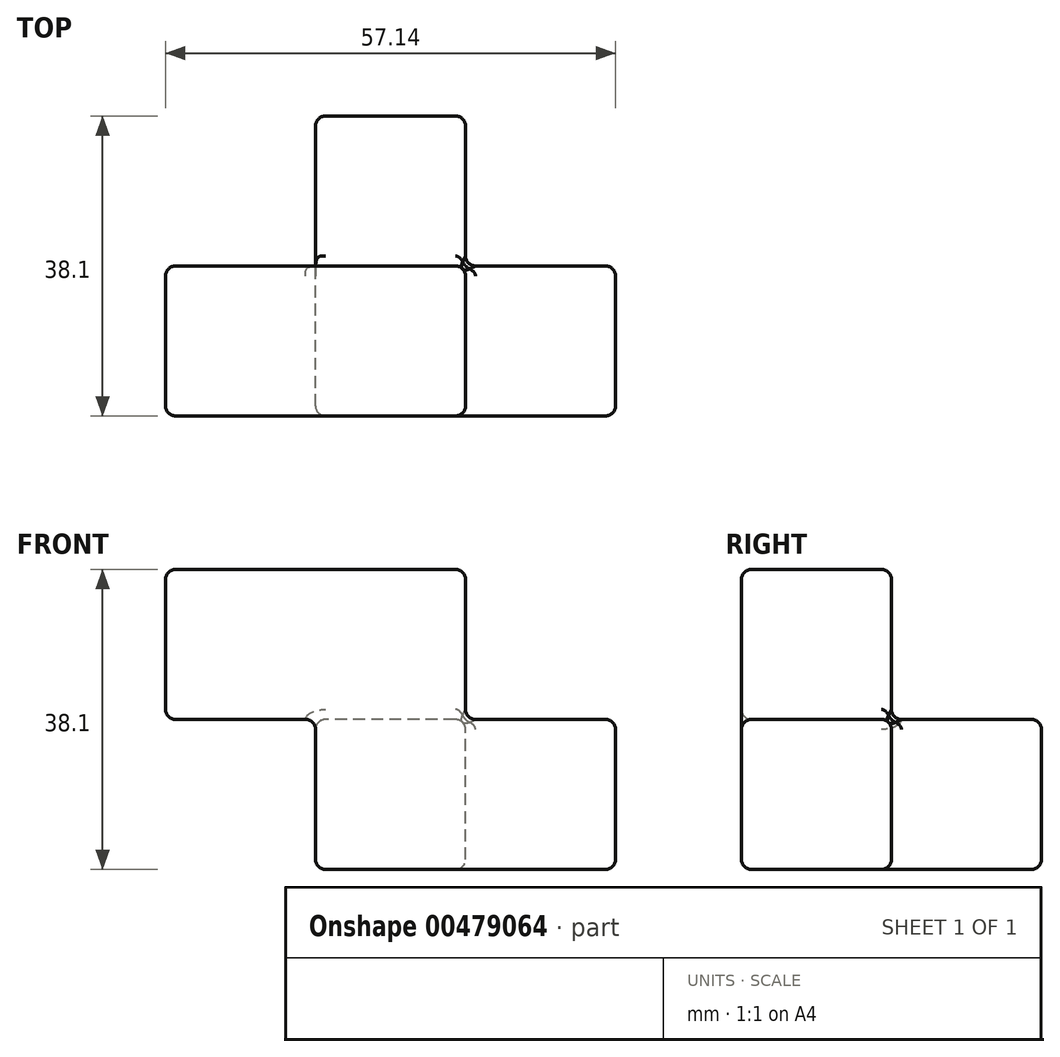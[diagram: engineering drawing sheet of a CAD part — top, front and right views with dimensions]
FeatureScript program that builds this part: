
annotation { "Feature Type Name" : "Feature", "Feature Type Description" : "" }
export const myFeature = defineFeature(function(context is Context, id is Id, definition is map)
    precondition{}
    {
        {
            var Q0;
            Q0=qCreatedBy(makeId("Top.planeOp"),FACE);
            var sketch = newSketch(context, id + "F0", { "sketchPlane" : qUnion([Q0])});
            skPoint(sketch, "E0.middle", {"position": v(0, 0) * mm});
            skLineSegment(sketch, "E1", {"start": v(-9.52, -9.52) * mm, "end": v(28.58, -9.52) * mm});
            skLineSegment(sketch, "E2", {"start": v(28.58, -9.52) * mm, "end": v(28.58, 9.53) * mm});
            skLineSegment(sketch, "E3", {"start": v(28.58, 9.53) * mm, "end": v(9.53, 9.53) * mm});
            skLineSegment(sketch, "E4", {"start": v(9.53, 9.53) * mm, "end": v(9.53, 28.58) * mm});
            skLineSegment(sketch, "E5", {"start": v(9.53, 28.58) * mm, "end": v(-9.52, 28.58) * mm});
            skLineSegment(sketch, "E6", {"start": v(-9.52, -9.52) * mm, "end": v(-9.52, 28.58) * mm});
            skSolve(sketch);
        }
        {
            var Q0;
            Q0 = qSketchRegion(id + "F0", true);
            extrude(context, id + "F1", {"entities" : qUnion([Q0]), "oppositeDirection" : true, "depth" : 19.05 * mm});
        }
        {
            var Q0;
            Q0=makeQuery(id+"F1.opExtrude","CAP_FACE",FACE,{"disambiguationData":[OSD([sQuery(id+"F0.wireOp",EDGE,"E1"),sQuery(id+"F0.wireOp",EDGE,"E2"),sQuery(id+"F0.wireOp",EDGE,"E3"),sQuery(id+"F0.wireOp",EDGE,"E4"),sQuery(id+"F0.wireOp",EDGE,"E5"),sQuery(id+"F0.wireOp",EDGE,"E6")])],"isStart":true});
            var sketch = newSketch(context, id + "F2", { "sketchPlane" : qUnion([Q0])});
            skLineSegment(sketch, "E7.bottom", {"start": v(9.53, 9.53) * mm, "end": v(-28.57, 9.53) * mm});
            skLineSegment(sketch, "E7.top", {"start": v(9.53, -9.52) * mm, "end": v(-28.57, -9.52) * mm});
            skLineSegment(sketch, "E7.left", {"start": v(9.53, 9.53) * mm, "end": v(9.53, -9.52) * mm});
            skLineSegment(sketch, "E7.right", {"start": v(-28.57, 9.53) * mm, "end": v(-28.57, -9.52) * mm});
            skSolve(sketch);
        }
        {
            var Q0;
            Q0 = qSketchRegion(id + "F2", true);
            extrude(context, id + "F3", {"entities" : qUnion([Q0]), "operationType" : NewBodyOperationType.ADD, "depth" : 19.05 * mm});
        }
        {
            var Q0;
            Q0=makeQuery(id+"F3.boolean.opBoolean","MERGE",FACE,{"derivedFrom":[makeQuery(id+"F1.opExtrude","SWEPT_FACE",FACE,{"disambiguationData":[OSD([sQuery(id+"F0.wireOp",EDGE,"E1")])]}),makeQuery(id+"F3.opExtrude","SWEPT_FACE",FACE,{"disambiguationData":[OSD([sQuery(id+"F2.wireOp",EDGE,"E7.top")])]})]});
            var Q1;
            Q1=makeQuery(id+"F3.opExtrude","SWEPT_FACE",FACE,{"disambiguationData":[OSD([sQuery(id+"F2.wireOp",EDGE,"E7.right")])]});
            var Q2;
            Q2=makeQuery(id+"F1.opExtrude","SWEPT_FACE",FACE,{"disambiguationData":[OSD([sQuery(id+"F0.wireOp",EDGE,"E6")])]});
            var Q3;
            Q3=makeQuery(id+"F3.opExtrude","CAP_FACE",FACE,{"disambiguationData":[OSD([sQuery(id+"F2.wireOp",EDGE,"E7.bottom"),sQuery(id+"F2.wireOp",EDGE,"E7.top"),sQuery(id+"F2.wireOp",EDGE,"E7.left"),sQuery(id+"F2.wireOp",EDGE,"E7.right")])],"isStart":true});
            var Q4;
            Q4=makeQuery(id+"F1.opExtrude","CAP_FACE",FACE,{"disambiguationData":[OSD([sQuery(id+"F0.wireOp",EDGE,"E1"),sQuery(id+"F0.wireOp",EDGE,"E2"),sQuery(id+"F0.wireOp",EDGE,"E3"),sQuery(id+"F0.wireOp",EDGE,"E4"),sQuery(id+"F0.wireOp",EDGE,"E5"),sQuery(id+"F0.wireOp",EDGE,"E6")])],"isStart":false});
            var Q5;
            Q5=makeQuery(id+"F1.opExtrude","SWEPT_FACE",FACE,{"disambiguationData":[OSD([sQuery(id+"F0.wireOp",EDGE,"E2")])]});
            var Q6;
            {var subQ0=sQuery(id+"F0.wireOp",EDGE,"E3");var subQ1=sQuery(id+"F0.wireOp",EDGE,"E2");var subQ2=sQuery(id+"F0.wireOp",EDGE,"E4");var subQ3=sQuery(id+"F0.wireOp",EDGE,"E1");var subQ4=makeQuery(id+"F1.opExtrude","CAP_FACE",FACE,{"disambiguationData":[OSD([subQ3,subQ1,subQ0,subQ2,sQuery(id+"F0.wireOp",EDGE,"E5"),sQuery(id+"F0.wireOp",EDGE,"E6")])],"isStart":true});Q6=makeQuery(id+"F3.boolean.opBoolean","SPLIT",FACE,{"disambiguationData":[TD([makeQuery(id+"F1.opExtrude","SWEPT_FACE",FACE,{"disambiguationData":[OSD([subQ3])]})])],"derivedFrom":subQ4});}
            var Q7;
            Q7=makeQuery(id+"F3.opExtrude","SWEPT_FACE",FACE,{"disambiguationData":[OSD([sQuery(id+"F2.wireOp",EDGE,"E7.left")])]});
            var Q8;
            Q8=makeQuery(id+"F1.opExtrude","SWEPT_FACE",FACE,{"disambiguationData":[OSD([sQuery(id+"F0.wireOp",EDGE,"E4")])]});
            var Q9;
            {var subQ0=sQuery(id+"F0.wireOp",EDGE,"E4");var subQ2=sQuery(id+"F0.wireOp",EDGE,"E3");var subQ3=sQuery(id+"F0.wireOp",EDGE,"E5");var subQ4=sQuery(id+"F0.wireOp",EDGE,"E6");var subQ5=makeQuery(id+"F1.opExtrude","CAP_FACE",FACE,{"disambiguationData":[OSD([sQuery(id+"F0.wireOp",EDGE,"E1"),sQuery(id+"F0.wireOp",EDGE,"E2"),subQ2,subQ0,subQ3,subQ4])],"isStart":true});Q9=makeQuery(id+"F3.boolean.opBoolean","SPLIT",FACE,{"disambiguationData":[TD([makeQuery(id+"F1.opExtrude","SWEPT_FACE",FACE,{"disambiguationData":[OSD([subQ3])]})])],"derivedFrom":subQ5});}
            var Q10;
            Q10=makeQuery(id+"F3.opExtrude","SWEPT_FACE",FACE,{"disambiguationData":[OSD([sQuery(id+"F2.wireOp",EDGE,"E7.bottom")])]});
            var Q11;
            Q11=makeQuery(id+"F3.opExtrude","CAP_FACE",FACE,{"disambiguationData":[OSD([sQuery(id+"F2.wireOp",EDGE,"E7.bottom"),sQuery(id+"F2.wireOp",EDGE,"E7.top"),sQuery(id+"F2.wireOp",EDGE,"E7.left"),sQuery(id+"F2.wireOp",EDGE,"E7.right")])],"isStart":false});
            fillet(context, id + "F4", {"entities" : qUnion([Q0, Q1, Q2, Q3, Q4, Q5, Q6, Q7, Q8, Q9, Q10, Q11]), "radius" : 1.27 * mm, "tangentPropagation" : true, "allowEdgeOverflow" : false});
        }
    });
